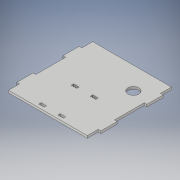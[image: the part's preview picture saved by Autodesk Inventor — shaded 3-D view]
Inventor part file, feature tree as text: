
AUTODESK INVENTOR PART (.ipt)
format: ipt  version: 2018 (Build 220112000, 112)  size: 142,848 bytes
history: native  units: in
note: dims shown in document units (in); Inventor stores cm internally (conversion verified against a paired STEP export)
features: extrude x2, sketch x2
ambient origin geometry x8: Origin, YZ Plane, XZ Plane, XY Plane, X Axis, Y Axis, Z Axis, Center Point
bodies: Solid1 (feature_tree)
feature tree (4):
  extrude  "Extrusion1"  Depth=0.5in
  extrude  "Extrusion2"  Depth=0.25in TaperAngle=0.0deg
  sketch  "Sketch1"  dims[d4=0.5in d6=0.5in]
  sketch  "Sketch2"  dims[d25=0.2188in d26=0.0in d27=0.25in d28=0.0in d29=0.2187in d31=0.219in]
